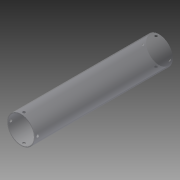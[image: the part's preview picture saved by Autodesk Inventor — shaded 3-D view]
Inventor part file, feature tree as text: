
AUTODESK INVENTOR PART (.ipt)
format: ipt  version: 2014 SP1 (Build 180222100, 222)  size: 150,528 bytes
history: native  units: in
note: dims shown in document units (in); Inventor stores cm internally (conversion verified against a paired STEP export)
features: extrude x3, sketch x3, plane x2, projected_geometry x1
ambient origin geometry x8: Origin, YZ Plane, XZ Plane, XY Plane, X Axis, Y Axis, Z Axis, Center Point
bodies: Solid1 (feature_tree)
feature tree (9):
  extrude  "Extrusion1"  Depth=1.875in
  plane  "Work Plane1"
  extrude  "Extrusion2"  Depth=5.0in
  plane  "Work Plane2"
  extrude  "Extrusion3"  Depth=0.2188in
  sketch  "Sketch1"  dims[d0=2.0in d1=1.875in]
  sketch  "Sketch2"  dims[d2=10.0in d3=0.0in d4=5.0in]
  projected_geometry  "Projected Loop1"
  sketch  "Sketch3"  dims[d5=0.19in d6=0.2188in d7=1.0in d8=2.0in d9=0.0in d10=5.0in d11=0.19in d12=0.2188in d13=1.0in d14=2.0in d15=0.0in]
